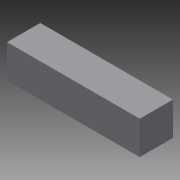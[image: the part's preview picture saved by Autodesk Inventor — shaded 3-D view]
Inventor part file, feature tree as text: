
AUTODESK INVENTOR PART (.ipt)
format: ipt  version: 2015 (Build 190159000, 159)  size: 68,608 bytes
history: native  units: in
note: dims shown in document units (in); Inventor stores cm internally (conversion verified against a paired STEP export)
features: extrude x1, sketch x1
ambient origin geometry x8: Origin, YZ Plane, XZ Plane, XY Plane, X Axis, Y Axis, Z Axis, Center Point
bodies: Solid1 (feature_tree)
feature tree (2):
  extrude  "Extrusion1"  Depth=0.75in
  sketch  "Sketch1"  dims[d0=0.75in d1=0.75in d2=3.0in d3=0.0in]
